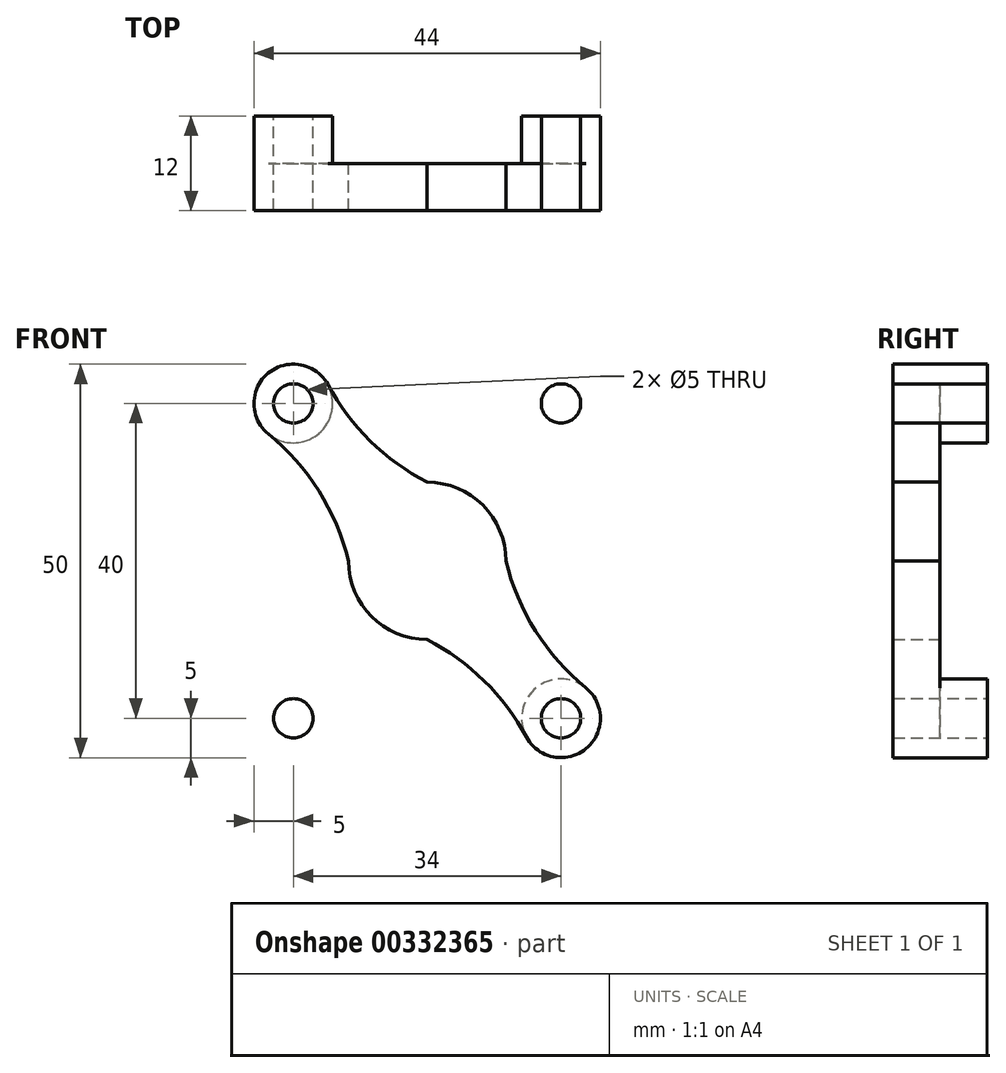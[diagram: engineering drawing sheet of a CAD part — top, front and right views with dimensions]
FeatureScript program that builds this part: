
annotation { "Feature Type Name" : "Feature", "Feature Type Description" : "" }
export const myFeature = defineFeature(function(context is Context, id is Id, definition is map)
    precondition{}
    {
        {
            var Q0;
            Q0=qCreatedBy(makeId("Front.planeOp"),FACE);
            var sketch = newSketch(context, id + "F0", { "sketchPlane" : qUnion([Q0])});
            skCircle(sketch, "E0", {"center": v(-17, 20) * mm, "radius": 2.5 * mm});
            skCircle(sketch, "E1.MirrorC", {"center": v(17, 20) * mm, "radius": 2.5 * mm});
            skCircle(sketch, "E2.MirrorC", {"center": v(17, -20) * mm, "radius": 2.5 * mm});
            skCircle(sketch, "E3.MirrorC", {"center": v(-17, -20) * mm, "radius": 2.5 * mm});
            skCircle(sketch, "E4", {"center": v(-17, 20) * mm, "radius": 5 * mm});
            skCircle(sketch, "E5.MirrorC", {"center": v(17, 20) * mm, "radius": 5 * mm});
            skCircle(sketch, "E6.MirrorC", {"center": v(-17, -20) * mm, "radius": 5 * mm});
            skCircle(sketch, "E7.MirrorC", {"center": v(17, -20) * mm, "radius": 5 * mm});
            skPoint(sketch, "E8.middle", {"position": v(0, 0) * mm});
            skCircle(sketch, "E9", {"center": v(0, 0) * mm, "radius": 10 * mm});
            skArc(sketch, "E10", {"start": v(-12.6, 22.38) * mm, "mid": v(-7.23, 15.24) * mm, "end": v(0, 10) * mm});
            skArc(sketch, "E11", {"start": v(-10, 0) * mm, "mid": v(-13.77, 8.9) * mm, "end": v(-20.16, 16.13) * mm});
            skArc(sketch, "E12.MirrorCS", {"start": v(12.6, 22.38) * mm, "mid": v(7.23, 15.24) * mm, "end": v(0, 10) * mm});
            skArc(sketch, "E13.MirrorCS", {"start": v(10, 0) * mm, "mid": v(13.77, 8.9) * mm, "end": v(20.16, 16.13) * mm});
            skArc(sketch, "E14.MirrorCS", {"start": v(-10, 0) * mm, "mid": v(-13.77, -8.9) * mm, "end": v(-20.16, -16.13) * mm});
            skArc(sketch, "E15.MirrorCS", {"start": v(-12.6, -22.38) * mm, "mid": v(-7.23, -15.24) * mm, "end": v(0, -10) * mm});
            skArc(sketch, "E16.MirrorCS", {"start": v(12.6, -22.38) * mm, "mid": v(7.23, -15.24) * mm, "end": v(0, -10) * mm});
            skArc(sketch, "E17.MirrorCS", {"start": v(10, 0) * mm, "mid": v(13.77, -8.9) * mm, "end": v(20.16, -16.13) * mm});
            skSolve(sketch);
        }
        {
            var Q0;
            Q0=makeQuery(id+"F0.imprint","IMPRINT",FACE,{"disambiguationData":[TD([[makeQuery(id+"F0.imprint","IMPRINT",EDGE,{"derivedFrom":sQuery(id+"F0.wireOp",EDGE,"E0")}),-1.0]])]});
            var Q1;
            Q1=makeQuery(id+"F0.imprint","IMPRINT",FACE,{"disambiguationData":[TD([[makeQuery(id+"F0.imprint","IMPRINT",EDGE,{"derivedFrom":sQuery(id+"F0.wireOp",EDGE,"E1.MirrorC")}),1.0]])]});
            var Q2;
            Q2=makeQuery(id+"F0.imprint","IMPRINT",FACE,{"disambiguationData":[TD([[makeQuery(id+"F0.imprint","IMPRINT",EDGE,{"derivedFrom":sQuery(id+"F0.wireOp",EDGE,"E2.MirrorC")}),-1.0]])]});
            var Q3;
            Q3=makeQuery(id+"F0.imprint","IMPRINT",FACE,{"disambiguationData":[TD([[makeQuery(id+"F0.imprint","IMPRINT",EDGE,{"derivedFrom":sQuery(id+"F0.wireOp",EDGE,"E3.MirrorC")}),1.0]])]});
            extrude(context, id + "F1", {"entities" : qUnion([Q0, Q1, Q2, Q3]), "depth" : 12 * mm, "offsetDistance" : 25 * mm});
        }
        {
            var Q0;
            Q0=makeQuery(id+"F0.imprint","IMPRINT",FACE,{"disambiguationData":[TD([[makeQuery(id+"F0.imprint","IMPRINT",EDGE,{"derivedFrom":sQuery(id+"F0.wireOp",EDGE,"E8.bottom")}),-1.0]])]});
            var Q1;
            {var subQ0=sQuery(id+"F0.wireOp",EDGE,"E10");Q1=makeQuery(id+"F0.imprint","IMPRINT",FACE,{"disambiguationData":[TD([[makeQuery(id+"F0.imprint","IMPRINT",EDGE,{"derivedFrom":subQ0}),-1.0]])]});}
            var Q2;
            {var subQ0=sQuery(id+"F0.wireOp",EDGE,"E9");var subQ1=makeQuery(id+"F0.imprint","INTERSECT",VERTEX,{"derivedFrom":[subQ0,sQuery(id+"F0.wireOp",EDGE,"E13.MirrorCS"),sQuery(id+"F0.wireOp",EDGE,"E17.MirrorCS")]});Q2=makeQuery(id+"F0.imprint","IMPRINT",FACE,{"disambiguationData":[TD([[makeQuery(id+"F0.imprint","IMPRINT",EDGE,{"disambiguationData":[TD([[subQ1,1.0]])],"derivedFrom":subQ0}),1.0]])]});}
            var Q3;
            {var subQ0=sQuery(id+"F0.wireOp",EDGE,"E14.MirrorCS");Q3=makeQuery(id+"F0.imprint","IMPRINT",FACE,{"disambiguationData":[TD([[makeQuery(id+"F0.imprint","IMPRINT",EDGE,{"derivedFrom":subQ0}),1.0]])]});}
            var Q4;
            {var subQ0=sQuery(id+"F0.wireOp",EDGE,"E16.MirrorCS");Q4=makeQuery(id+"F0.imprint","IMPRINT",FACE,{"disambiguationData":[TD([[makeQuery(id+"F0.imprint","IMPRINT",EDGE,{"derivedFrom":subQ0}),-1.0]])]});}
            var Q5;
            {var subQ3=sQuery(id+"F0.wireOp",EDGE,"E12.MirrorCS");Q5=makeQuery(id+"F0.imprint","IMPRINT",FACE,{"disambiguationData":[TD([[makeQuery(id+"F0.imprint","IMPRINT",EDGE,{"derivedFrom":subQ3}),1.0]])]});}
            extrude(context, id + "F2", {"entities" : qUnion([Q0, Q1, Q2, Q3, Q4, Q5]), "operationType" : NewBodyOperationType.ADD, "depth" : 12 * mm, "offsetDistance" : 25 * mm, "hasSecondDirection" : true, "secondDirectionOppositeDirection" : false, "secondDirectionDepth" : 6 * mm});
        }
    });
